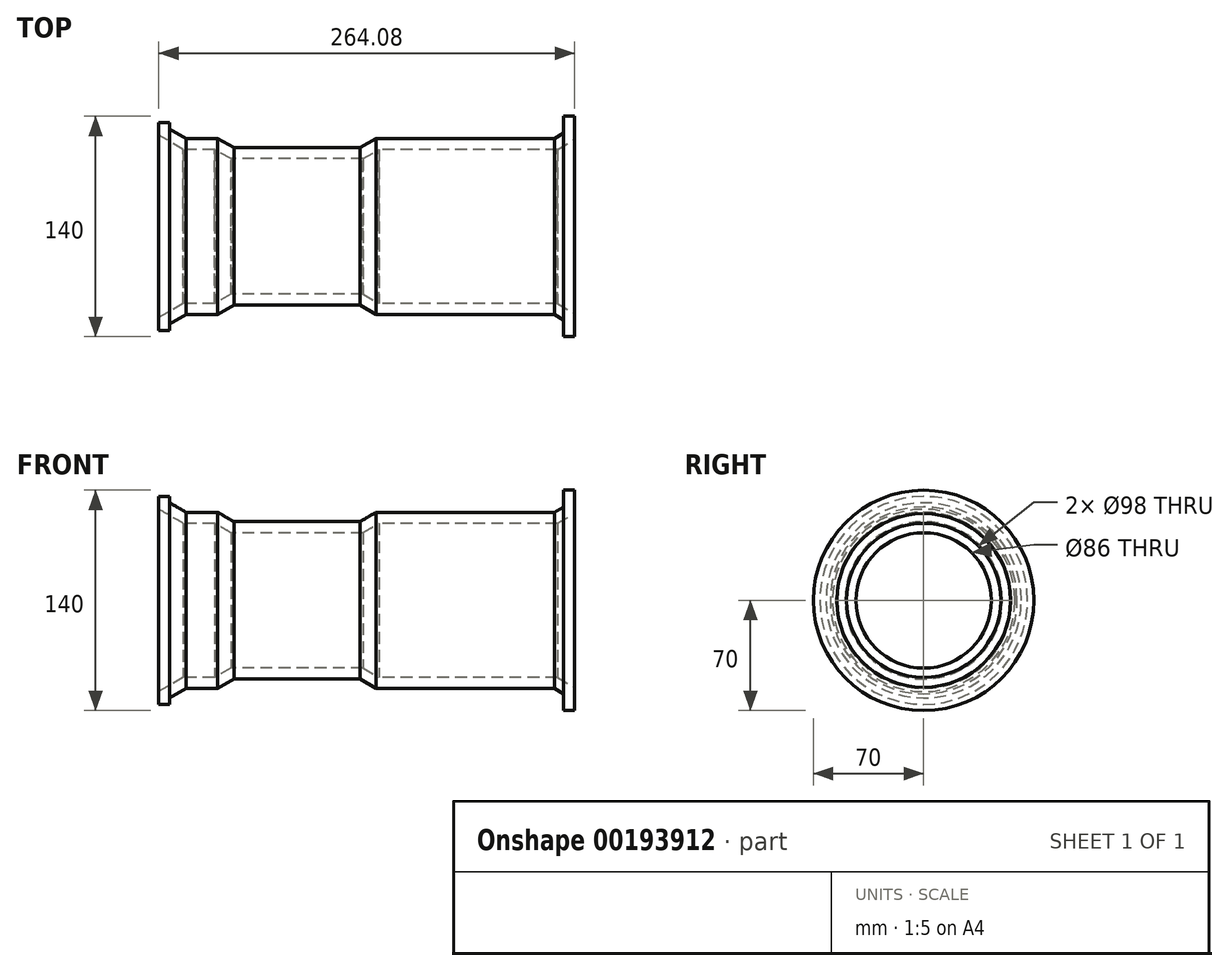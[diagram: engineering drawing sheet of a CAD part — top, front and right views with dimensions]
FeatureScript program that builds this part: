
annotation { "Feature Type Name" : "Feature", "Feature Type Description" : "" }
export const myFeature = defineFeature(function(context is Context, id is Id, definition is map)
    precondition{}
    {
        {
            var Q0;
            Q0=qCreatedBy(makeId("Front.planeOp"),FACE);
            var sketch = newSketch(context, id + "F0", { "sketchPlane" : qUnion([Q0])});
            skLineSegment(sketch, "E0", {"start": v(-105.55, 66) * mm, "end": v(-105.55, 62) * mm});
            skLineSegment(sketch, "E1", {"start": v(-105.55, 62) * mm, "end": v(-95.16, 56) * mm});
            skLineSegment(sketch, "E2", {"start": v(-95.16, 56) * mm, "end": v(-75.16, 56) * mm});
            skLineSegment(sketch, "E3", {"start": v(-75.16, 56) * mm, "end": v(-64.77, 50) * mm});
            skLineSegment(sketch, "E4", {"start": v(-64.77, 50) * mm, "end": v(15.23, 50) * mm});
            skLineSegment(sketch, "E5", {"start": v(15.23, 50) * mm, "end": v(25.62, 56) * mm});
            skLineSegment(sketch, "E6", {"start": v(25.62, 56) * mm, "end": v(138.86, 56) * mm});
            skLineSegment(sketch, "E7", {"start": v(138.86, 56) * mm, "end": v(144.67, 59.36) * mm});
            skLineSegment(sketch, "E8", {"start": v(144.67, 59.36) * mm, "end": v(144.67, 66) * mm});
            skLineSegment(sketch, "E9.1", {"start": v(140.74, 49) * mm, "end": v(151.38, 55.14) * mm});
            skLineSegment(sketch, "E9.2", {"start": v(27.5, 49) * mm, "end": v(140.74, 49) * mm});
            skLineSegment(sketch, "E9.3", {"start": v(17.1, 43) * mm, "end": v(27.5, 49) * mm});
            skLineSegment(sketch, "E9.4", {"start": v(-66.65, 43) * mm, "end": v(17.1, 43) * mm});
            skLineSegment(sketch, "E9.5", {"start": v(-112.55, 66) * mm, "end": v(-112.55, 57.96) * mm});
            skLineSegment(sketch, "E9.6", {"start": v(-112.55, 57.96) * mm, "end": v(-97.04, 49) * mm});
            skLineSegment(sketch, "E9.7", {"start": v(-97.04, 49) * mm, "end": v(-77.04, 49) * mm});
            skLineSegment(sketch, "E9.8", {"start": v(-77.04, 49) * mm, "end": v(-66.65, 43) * mm});
            skLineSegment(sketch, "E10", {"start": v(-112.55, 66) * mm, "end": v(-105.55, 66) * mm});
            skLineSegment(sketch, "E11", {"start": v(144.67, 66) * mm, "end": v(144.67, 70) * mm});
            skLineSegment(sketch, "E12", {"start": v(144.67, 70) * mm, "end": v(151.53, 70) * mm});
            skLineSegment(sketch, "E13", {"start": v(151.53, 70) * mm, "end": v(151.38, 55.14) * mm});
            skLineSegment(sketch, "E14", {"start": v(-120.05, 0) * mm, "end": v(220.8, 0) * mm, "construction": true});
            skSolve(sketch);
        }
        {
            var Q0;
            Q0=makeQuery(id+"F0.imprint","IMPRINT",FACE,{"disambiguationData":[TD([[makeQuery(id+"F0.imprint","IMPRINT",EDGE,{"derivedFrom":sQuery(id+"F0.wireOp",EDGE,"E0")}),-1.0]])]});
            var Q1;
            Q1=sQuery(id+"F0.wireOp",EDGE,"E14");
            revolve(context, id + "F1", {"entities" : qUnion([Q0]), "axis" : qUnion([Q1]), "revolveType" : RevolveType.FULL});
        }
    });
